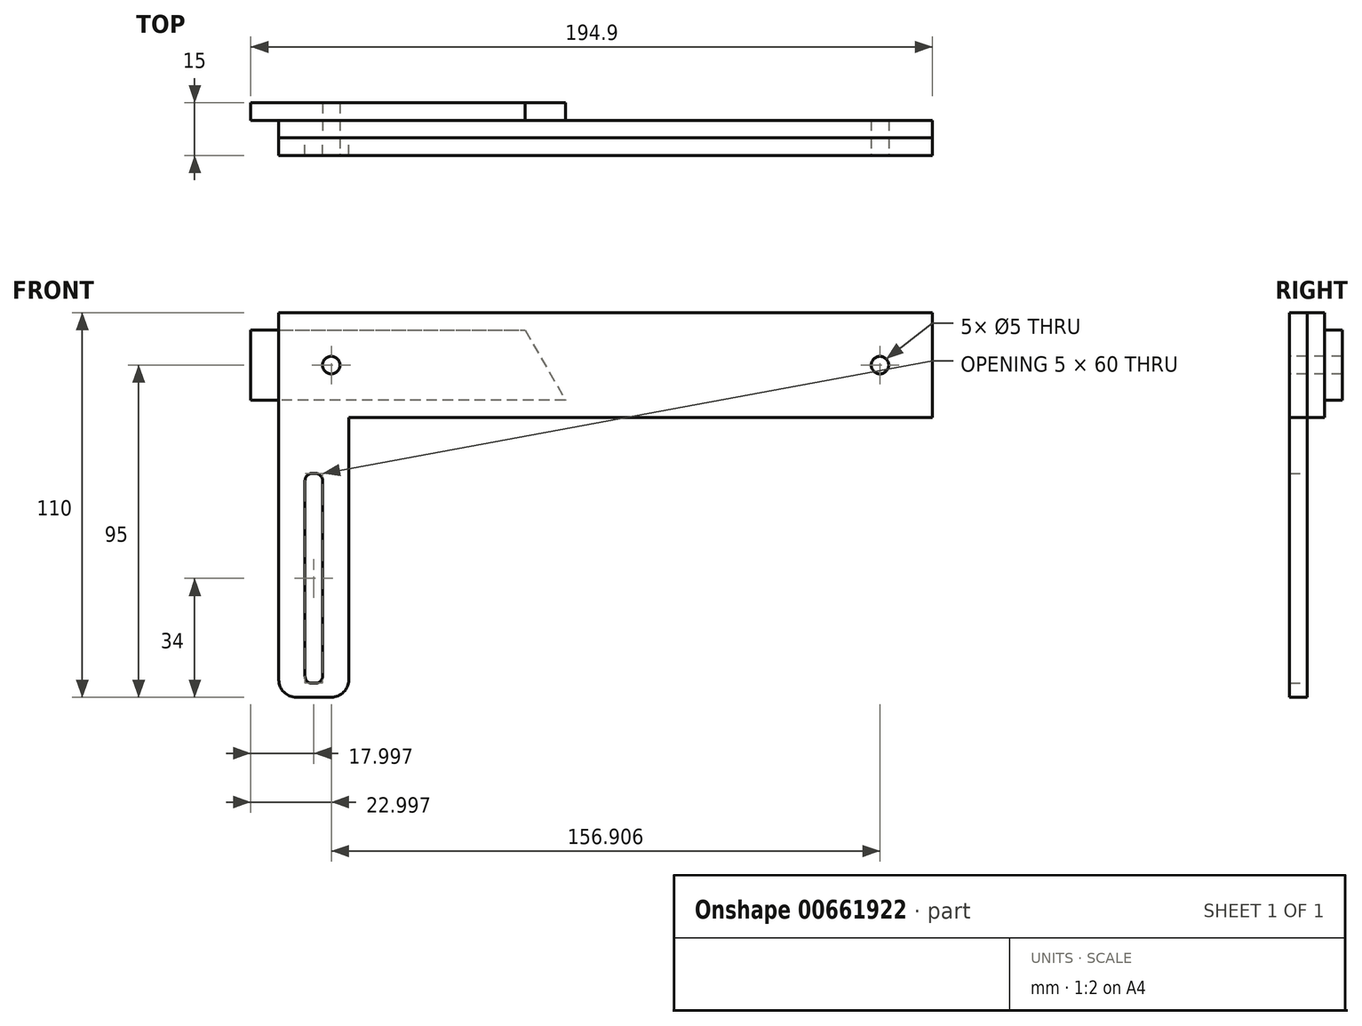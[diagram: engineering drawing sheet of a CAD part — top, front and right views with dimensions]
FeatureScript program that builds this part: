
annotation { "Feature Type Name" : "Feature", "Feature Type Description" : "" }
export const myFeature = defineFeature(function(context is Context, id is Id, definition is map)
    precondition{}
    {
        {
            var Q0;
            Q0=qCreatedBy(makeId("Front.planeOp"),FACE);
            var sketch = newSketch(context, id + "F0", { "sketchPlane" : qUnion([Q0])});
            skLineSegment(sketch, "E0", {"start": v(-101.45, 0) * mm, "end": v(-101.45, 20) * mm});
            skLineSegment(sketch, "E1", {"start": v(-101.45, 20) * mm, "end": v(-23, 20) * mm});
            skLineSegment(sketch, "E2", {"start": v(-23, 20) * mm, "end": v(-11.45, 0) * mm});
            skLineSegment(sketch, "E3", {"start": v(-11.45, 0) * mm, "end": v(-101.45, 0) * mm});
            skSolve(sketch);
        }
        {
            var Q0;
            Q0 = qSketchRegion(id + "F0", true);
            extrude(context, id + "F1", {"entities" : qUnion([Q0]), "depth" : 5 * mm, "offsetDistance" : 25 * mm});
        }
        {
            var Q0;
            Q0=makeQuery(id+"F1.opExtrude","CAP_FACE",FACE,{"disambiguationData":[OSD([sQuery(id+"F0.wireOp",EDGE,"E0"),sQuery(id+"F0.wireOp",EDGE,"E1"),sQuery(id+"F0.wireOp",EDGE,"E2"),sQuery(id+"F0.wireOp",EDGE,"E3")])],"isStart":false});
            var sketch = newSketch(context, id + "F2", { "sketchPlane" : qUnion([Q0])});
            skPoint(sketch, "E4", {"position": v(0, 0) * mm});
            skLineSegment(sketch, "E5.bottom", {"start": v(-93.45, 25) * mm, "end": v(93.45, 25) * mm});
            skLineSegment(sketch, "E5.top", {"start": v(-93.45, -5) * mm, "end": v(93.45, -5) * mm});
            skLineSegment(sketch, "E5.left", {"start": v(-93.45, 25) * mm, "end": v(-93.45, -5) * mm});
            skPoint(sketch, "E6", {"position": v(0, -5) * mm});
            skLineSegment(sketch, "E7", {"start": v(93.45, 25) * mm, "end": v(93.45, -5) * mm});
            skLineSegment(sketch, "E8", {"start": v(0, -5) * mm, "end": v(0, 0) * mm, "construction": true});
            skSolve(sketch);
        }
        {
            var Q0;
            Q0 = qSketchRegion(id + "F2", true);
            extrude(context, id + "F3", {"entities" : qUnion([Q0]), "depth" : 5 * mm, "offsetDistance" : 25 * mm});
        }
        {
            var Q0;
            Q0=makeQuery(id+"F3.opExtrude","CAP_FACE",FACE,{"disambiguationData":[OSD([sQuery(id+"F2.wireOp",EDGE,"E5.bottom"),sQuery(id+"F2.wireOp",EDGE,"E5.top"),sQuery(id+"F2.wireOp",EDGE,"E5.left"),sQuery(id+"F2.wireOp",EDGE,"E7")])],"isStart":false});
            var sketch = newSketch(context, id + "F4", { "sketchPlane" : qUnion([Q0])});
            skLineSegment(sketch, "E9.bottom", {"start": v(-93.45, 25) * mm, "end": v(93.45, 25) * mm});
            skLineSegment(sketch, "E9.top", {"start": v(-93.45, -5) * mm, "end": v(93.45, -5) * mm});
            skLineSegment(sketch, "E9.left", {"start": v(-93.45, 25) * mm, "end": v(-93.45, -5) * mm});
            skLineSegment(sketch, "E9.right", {"start": v(93.45, 25) * mm, "end": v(93.45, -5) * mm});
            skLineSegment(sketch, "E10.bottom", {"start": v(-73.45, -5) * mm, "end": v(-93.45, -5) * mm});
            skLineSegment(sketch, "E10.top", {"start": v(-78.45, -85) * mm, "end": v(-88.45, -85) * mm});
            skLineSegment(sketch, "E10.left", {"start": v(-73.45, -5) * mm, "end": v(-73.45, -80) * mm});
            skLineSegment(sketch, "E10.right", {"start": v(-93.45, -5) * mm, "end": v(-93.45, -80) * mm});
            skPoint(sketch, "E11", {"position": v(-83.45, -85) * mm});
            skLineSegment(sketch, "E12.bottom", {"start": v(-82.95, -21) * mm, "end": v(-83.95, -21) * mm});
            skLineSegment(sketch, "E12.top", {"start": v(-82.95, -81) * mm, "end": v(-83.95, -81) * mm});
            skLineSegment(sketch, "E12.left", {"start": v(-80.95, -23) * mm, "end": v(-80.95, -79) * mm});
            skLineSegment(sketch, "E12.right", {"start": v(-85.95, -23) * mm, "end": v(-85.95, -79) * mm});
            skPoint(sketch, "E12.middle", {"position": v(-83.45, -51) * mm});
            skLineSegment(sketch, "E13", {"start": v(-83.45, -85) * mm, "end": v(-83.45, -51) * mm, "construction": true});
            skPoint(sketch, "E14.visualSharp", {"position": v(-80.95, -81) * mm});
            skArc(sketch, "E14.filletArc", {"start": v(-82.95, -81) * mm, "mid": v(-81.54, -80.41) * mm, "end": v(-80.95, -79) * mm});
            skPoint(sketch, "E15.visualSharp", {"position": v(-85.95, -81) * mm});
            skArc(sketch, "E15.filletArc", {"start": v(-85.95, -79) * mm, "mid": v(-85.37, -80.41) * mm, "end": v(-83.95, -81) * mm});
            skPoint(sketch, "E16.visualSharp", {"position": v(-80.95, -21) * mm});
            skArc(sketch, "E16.filletArc", {"start": v(-80.95, -23) * mm, "mid": v(-81.54, -21.59) * mm, "end": v(-82.95, -21) * mm});
            skPoint(sketch, "E17.visualSharp", {"position": v(-85.95, -21) * mm});
            skArc(sketch, "E17.filletArc", {"start": v(-83.95, -21) * mm, "mid": v(-85.37, -21.59) * mm, "end": v(-85.95, -23) * mm});
            skPoint(sketch, "E18", {"position": v(-83.45, -21) * mm});
            skPoint(sketch, "E19", {"position": v(-83.45, -81) * mm});
            skLineSegment(sketch, "E20", {"start": v(-83.45, -81) * mm, "end": v(-83.45, -21) * mm, "construction": true});
            skPoint(sketch, "E21.visualSharp", {"position": v(-73.45, -85) * mm});
            skArc(sketch, "E21.filletArc", {"start": v(-78.45, -85) * mm, "mid": v(-74.92, -83.54) * mm, "end": v(-73.45, -80) * mm});
            skPoint(sketch, "E22.visualSharp", {"position": v(-93.45, -85) * mm});
            skArc(sketch, "E22.filletArc", {"start": v(-93.45, -80) * mm, "mid": v(-91.99, -83.54) * mm, "end": v(-88.45, -85) * mm});
            skSolve(sketch);
        }
        {
            var Q0;
            Q0 = qSketchRegion(id + "F4", true);
            extrude(context, id + "F5", {"entities" : qUnion([Q0]), "depth" : 5 * mm, "offsetDistance" : 25 * mm});
        }
        {
            var Q0;
            Q0=makeQuery(id+"F5.opExtrude","CAP_FACE",FACE,{"disambiguationData":[OSD([sQuery(id+"F4.wireOp",EDGE,"E9.bottom"),sQuery(id+"F4.wireOp",EDGE,"E9.top"),sQuery(id+"F4.wireOp",EDGE,"E9.left"),sQuery(id+"F4.wireOp",EDGE,"E9.right"),sQuery(id+"F4.wireOp",EDGE,"E10.top"),sQuery(id+"F4.wireOp",EDGE,"E10.left"),sQuery(id+"F4.wireOp",EDGE,"E10.right"),sQuery(id+"F4.wireOp",EDGE,"iSuBmkse-nLkB-Q0ET-p3nw-THPlKKKo1YNX")])],"isStart":false});
            var sketch = newSketch(context, id + "F6", { "sketchPlane" : qUnion([Q0])});
            skCircle(sketch, "E23", {"center": v(-78.45, 10) * mm, "radius": 2.5 * mm});
            skLineSegment(sketch, "E24", {"start": v(0, 0) * mm, "end": v(0, 32.78) * mm, "construction": true});
            skCircle(sketch, "E25.MirrorC", {"center": v(78.45, 10) * mm, "radius": 2.5 * mm});
            skPoint(sketch, "E26", {"position": v(-93.45, 10) * mm});
            skLineSegment(sketch, "E27", {"start": v(-93.45, 10) * mm, "end": v(-78.45, 10) * mm, "construction": true});
            skSolve(sketch);
        }
        {
            var Q0;
            Q0 = qSketchRegion(id + "F6", true);
            extrude(context, id + "F7", {"entities" : qUnion([Q0]), "operationType" : NewBodyOperationType.REMOVE, "endBound" : BoundingType.THROUGH_ALL, "oppositeDirection" : true, "depth" : 25 * mm, "offsetDistance" : 25 * mm});
        }
    });
